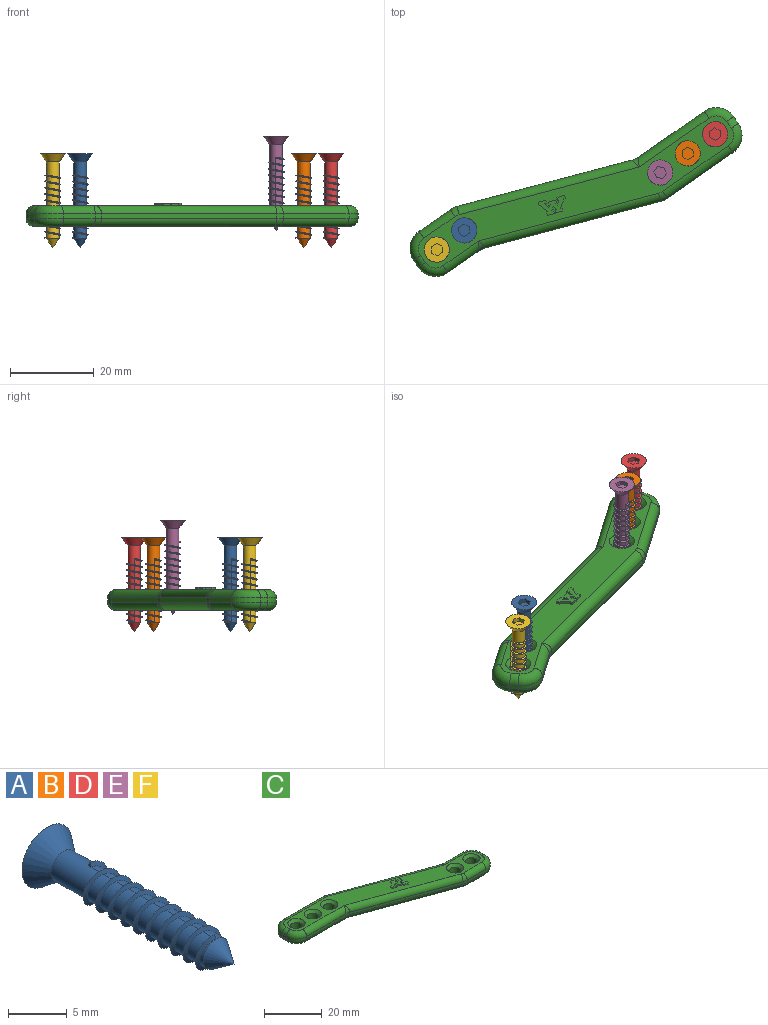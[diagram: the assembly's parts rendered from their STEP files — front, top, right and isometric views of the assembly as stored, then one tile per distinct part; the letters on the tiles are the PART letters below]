
ASSEMBLY  parts=6 mates=5
PART A: 25 faces, bbox 6x22.5x6 mm
  f0: plane 6x6mm, normal (0,1,0), area 22.4mm2, adj f12,f18,f19,f20,f21,f22,f23
  f1: cylinder r=1.5mm len=4.5mm, axis (0,1,0), area 35.3mm2, adj f2,f12,f13,f15
  f2: cylinder r=1.5mm len=3mm, axis (0,1,0), area 11.3mm2, adj f1,f3,f15,f16
  f3: cylinder r=1.5mm len=3mm, axis (0,1,0), area 11.3mm2, adj f2,f4,f15,f16
  f4: cylinder r=1.5mm len=3mm, axis (0,1,0), area 11.3mm2, adj f3,f5,f15,f16
  f5: cylinder r=1.5mm len=3mm, axis (0,1,0), area 11.3mm2, adj f4,f6,f15,f16
  f6: cylinder r=1.5mm len=3mm, axis (0,1,0), area 11.3mm2, adj f5,f7,f15,f16
  f7: cylinder r=1.5mm len=3mm, axis (0,1,0), area 11.3mm2, adj f6,f8,f15,f16
  f8: cylinder r=1.5mm len=3mm, axis (0,1,0), area 11.3mm2, adj f7,f9,f15,f16
  f9: cylinder r=1.5mm len=3mm, axis (0,1,0), area 11.3mm2, adj f8,f10,f15,f16
  f10: cylinder r=1.5mm len=3mm, axis (0,1,0), area 11.3mm2, adj f9,f11,f15,f16
  f11: cylinder r=1.5mm len=3mm, axis (0,1,0), area 7.1mm2, adj f10,f14,f16,f17
  f12: cone r=1.5mm half-angle=36.9deg, axis (0,1,0), area 35.3mm2, adj f0,f1
  f13: plane 0.4x0.3mm, normal (-1,0,0), area 0.1mm2, adj f1,f15,f16
  f14: plane 0.4x0.3mm, normal (1,0,0), area 0.1mm2, adj f11,f15,f16
  f15: bspline ~15.15x4.39mm, area 45.9mm2, adj f1,f2,f3,f4,f5,f6,f7,f8
  f16: bspline ~15.15x4.39mm, area 46mm2, adj f2,f3,f4,f5,f6,f7,f8,f9
  f17: cone r=1.5mm half-angle=34.3deg, axis (0,1,0), area 12.5mm2, adj f11
  f18: plane 1.5x1mm, normal (0,0,-1), area 1.5mm2, adj f0,f19,f23,f24
  f19: plane 1.3x1mm, normal (-0.87,0,-0.5), area 1.5mm2, adj f0,f18,f20,f24
  f20: plane 1.3x1mm, normal (-0.87,0,0.5), area 1.5mm2, adj f0,f19,f21,f24
  f21: plane 1.5x1mm, normal (0,0,1), area 1.5mm2, adj f0,f20,f22,f24
  f22: plane 1.3x1mm, normal (0.87,0,0.5), area 1.5mm2, adj f0,f21,f23,f24
  f23: plane 1.3x1mm, normal (0.87,0,-0.5), area 1.5mm2, adj f0,f18,f22,f24
  f24: plane 3x2.6mm, normal (0,1,0), area 5.8mm2, adj f18,f19,f20,f21,f22,f23
PART B: same geometry as A
PART C: 94 faces, bbox 83.1x28.2x5.6 mm
  f0: plane 78.29x23.39mm, normal (0,0,1), area 452.6mm2, adj f23,f24,f25,f26,f27,f28,f29,f30
  f1: plane 78.29x23.39mm, normal (0,0,-1), area 544.8mm2, adj f10,f11,f12,f13,f14,f15,f16,f17
  f2: plane 2x1mm, normal (-1,0,0), area 2mm2, adj f18,f26,f44,f47
  f3: plane 19.12x1mm, normal (0,-1,0), area 19.1mm2, adj f16,f24,f47,f50
  f4: plane 40.63x14.79mm, normal (-0.34,-0.94,0), area 43.2mm2, adj f15,f23,f41,f50
  f5: plane 9.12x1mm, normal (0,-1,0), area 9.1mm2, adj f17,f25,f38,f41
  f6: plane 2x1mm, normal (1,0,0), area 2mm2, adj f19,f27,f35,f38
  f7: plane 9.12x1mm, normal (0,1,0), area 9.1mm2, adj f21,f29,f35,f53
  f8: plane 40.63x14.79mm, normal (0.34,0.94,0), area 43.2mm2, adj f22,f30,f32,f53
  f9: plane 19.12x1mm, normal (0,1,0), area 19.1mm2, adj f20,f28,f32,f44
  f10: cylinder r=2mm len=4mm, axis (0,0,1), area 50.3mm2, adj f1,f55
  f11: cylinder r=2mm len=4mm, axis (0,0,1), area 50.3mm2, adj f1,f58
  f12: cylinder r=2mm len=4mm, axis (0,0,1), area 50.3mm2, adj f1,f59
  f13: cylinder r=2mm len=4mm, axis (0,0,1), area 50.3mm2, adj f1,f56
  f14: cylinder r=2mm len=4mm, axis (0,0,1), area 50.3mm2, adj f1,f57
  f15: cylinder r=2mm len=42.47mm, axis (0.94,-0.34,0), area 137.2mm2, adj f1,f4,f42,f49
  f16: cylinder r=2mm len=20.35mm, axis (1,0,0), area 61.5mm2, adj f1,f3,f48,f49
  f17: cylinder r=2mm len=9.12mm, axis (1,0,0), area 28.6mm2, adj f1,f5,f39,f42
  f18: cylinder r=2mm len=2mm, axis (0,-1,0), area 6.3mm2, adj f1,f2,f45,f48
  f19: cylinder r=2mm len=2mm, axis (0,1,0), area 6.3mm2, adj f1,f6,f36,f39
  f20: cylinder r=2mm len=19.12mm, axis (-1,0,0), area 60.1mm2, adj f1,f9,f33,f45
  f21: cylinder r=2mm len=10.35mm, axis (-1,0,0), area 30.1mm2, adj f1,f7,f36,f52
  f22: cylinder r=2mm len=42.47mm, axis (-0.94,0.34,0), area 137.2mm2, adj f1,f8,f33,f52
  f23: cylinder r=2mm len=42.47mm, axis (-0.94,0.34,0), area 137.2mm2, adj f0,f4,f40,f51
  f24: cylinder r=2mm len=20.35mm, axis (-1,0,0), area 61.5mm2, adj f0,f3,f46,f51
  f25: cylinder r=2mm len=9.12mm, axis (-1,0,0), area 28.6mm2, adj f0,f5,f37,f40
  f26: cylinder r=2mm len=2mm, axis (0,1,0), area 6.3mm2, adj f0,f2,f43,f46
  f27: cylinder r=2mm len=2mm, axis (0,-1,0), area 6.3mm2, adj f0,f6,f34,f37
  f28: cylinder r=2mm len=19.12mm, axis (1,0,0), area 60.1mm2, adj f0,f9,f31,f43
  f29: cylinder r=2mm len=10.35mm, axis (1,0,0), area 30.1mm2, adj f0,f7,f34,f54
  f30: cylinder r=2mm len=42.47mm, axis (0.94,-0.34,0), area 137.2mm2, adj f0,f8,f31,f54
  f31: torus R=3mm, axis (0,0,1), area 4.7mm2, adj f0,f28,f30,f32
  f32: cylinder r=5mm len=1.71mm, axis (0,0,-1), area 1.7mm2, adj f8,f9,f31,f33
  f33: torus R=3mm, axis (0,0,1), area 4.7mm2, adj f1,f20,f22,f32
  f34: torus R=3mm, axis (0,0,1), area 21.1mm2, adj f0,f27,f29,f35
  f35: cylinder r=5mm len=5mm, axis (0,0,1), area 7.9mm2, adj f6,f7,f34,f36
  f36: torus R=3mm, axis (0,0,1), area 21.1mm2, adj f1,f19,f21,f35
  f37: torus R=3mm, axis (0,0,1), area 21.1mm2, adj f0,f25,f27,f38
  f38: cylinder r=5mm len=5mm, axis (0,0,-1), area 7.9mm2, adj f5,f6,f37,f39
  f39: torus R=3mm, axis (0,0,1), area 21.1mm2, adj f1,f17,f19,f38
  f40: torus R=3mm, axis (0,0,1), area 4.7mm2, adj f0,f23,f25,f41
  f41: cylinder r=5mm len=1.71mm, axis (0,0,-1), area 1.7mm2, adj f4,f5,f40,f42
  f42: torus R=3mm, axis (0,0,1), area 4.7mm2, adj f1,f15,f17,f41
  f43: torus R=3mm, axis (0,0,1), area 21.1mm2, adj f0,f26,f28,f44
  f44: cylinder r=5mm len=5mm, axis (0,0,1), area 7.9mm2, adj f2,f9,f43,f45
  f45: torus R=3mm, axis (0,0,1), area 21.1mm2, adj f1,f18,f20,f44
  f46: torus R=3mm, axis (0,0,1), area 21.1mm2, adj f0,f24,f26,f47
  f47: cylinder r=5mm len=5mm, axis (0,0,-1), area 7.9mm2, adj f2,f3,f46,f48
  f48: torus R=3mm, axis (0,0,1), area 21.1mm2, adj f1,f16,f18,f47
  f49: bspline ~2.3x2.26mm, area 3.5mm2, adj f15,f16,f50
  f50: cylinder r=5mm len=1.71mm, axis (0,0,1), area 1.7mm2, adj f3,f4,f49,f51
  f51: bspline ~2.3x2.26mm, area 3.5mm2, adj f23,f24,f50
  f52: bspline ~2.3x2.26mm, area 3.5mm2, adj f21,f22,f53
  f53: cylinder r=5mm len=1.71mm, axis (0,0,1), area 1.7mm2, adj f7,f8,f52,f54
  f54: bspline ~2.3x2.26mm, area 3.5mm2, adj f29,f30,f53
  f55: cone r=2mm half-angle=45deg, axis (0,0,1), area 22.2mm2, adj f0,f10
  f56: cone r=2mm half-angle=45deg, axis (0,0,1), area 22.2mm2, adj f0,f13
  f57: cone r=2mm half-angle=45deg, axis (0,0,1), area 22.2mm2, adj f0,f14
  f58: cone r=2mm half-angle=45deg, axis (0,0,1), area 22.2mm2, adj f0,f11
  f59: cone r=2mm half-angle=45deg, axis (0,0,1), area 22.2mm2, adj f0,f12
  f60: plane 2.01x1.45mm, normal (-0.59,0.81,0), area 1.5mm2, adj f0,f61,f92,f93
  f61: plane 0.6x0.38mm, normal (0.39,0.92,0), area 0.2mm2, adj f0,f60,f62,f93
  f62: plane 0.75x0.6mm, normal (-0.94,0.33,0), area 0.5mm2, adj f0,f61,f63,f93
  f63: plane 1.79x0.65mm, normal (-0.34,-0.94,0), area 1.1mm2, adj f0,f62,f64,f93
  f64: plane 0.75x0.6mm, normal (0.94,-0.34,0), area 0.5mm2, adj f0,f63,f65,f93
  f65: plane 0.6x0.27mm, normal (0.34,0.94,0), area 0.2mm2, adj f0,f64,f66,f93
  f66: plane 1.01x0.73mm, normal (0.59,-0.81,0), area 0.8mm2, adj f0,f65,f67,f93
  f67: plane 0.6x0.51mm, normal (-0.98,-0.2,0), area 0.3mm2, adj f0,f66,f68,f93
  f68: plane 0.6x0.36mm, normal (0.34,0.94,0), area 0.2mm2, adj f0,f67,f69,f93
  f69: plane 0.79x0.6mm, normal (-0.94,0.34,0), area 0.5mm2, adj f0,f68,f70,f93
  f70: plane 1.91x0.69mm, normal (-0.34,-0.94,0), area 1.2mm2, adj f0,f69,f71,f93
  f71: plane 0.69x0.6mm, normal (0.94,-0.34,0), area 0.4mm2, adj f0,f70,f72,f93
  f72: plane 0.6x0.27mm, normal (0.34,0.94,0), area 0.2mm2, adj f0,f71,f73,f93
  f73: plane 0.65x0.6mm, normal (0.6,-0.8,0), area 0.5mm2, adj f0,f72,f74,f93
  f74: plane 1.43x0.6mm, normal (-0.98,-0.17,0), area 0.9mm2, adj f0,f73,f75,f93
  f75: plane 0.6x0.46mm, normal (0.34,0.94,0), area 0.3mm2, adj f0,f74,f76,f93
  f76: plane 0.68x0.6mm, normal (-0.94,0.34,0), area 0.4mm2, adj f0,f75,f77,f93
  f77: plane 1.79x0.65mm, normal (-0.34,-0.94,0), area 1.1mm2, adj f0,f76,f78,f93
  f78: plane 0.84x0.6mm, normal (0.94,-0.34,0), area 0.5mm2, adj f0,f77,f79,f93
  f79: plane 0.6x0.31mm, normal (0.34,0.94,0), area 0.2mm2, adj f0,f78,f80,f93
  f80: plane 2.21x0.61mm, normal (0.96,0.27,0), area 1.4mm2, adj f0,f79,f81,f93
  f81: plane 0.6x0.3mm, normal (-0.51,-0.86,0), area 0.2mm2, adj f0,f80,f82,f93
  f82: plane 0.84x0.6mm, normal (0.94,-0.34,0), area 0.5mm2, adj f0,f81,f83,f93
  f83: plane 1.67x0.61mm, normal (0.34,0.94,0), area 1.1mm2, adj f0,f82,f84,f93
  f84: plane 0.85x0.6mm, normal (-0.94,0.34,0), area 0.5mm2, adj f0,f83,f85,f93
  f85: plane 0.6x0.41mm, normal (-0.34,-0.94,0), area 0.3mm2, adj f0,f84,f86,f93
  f86: plane 0.81x0.6mm, normal (-0.59,0.81,0), area 0.6mm2, adj f0,f85,f87,f93
  f87: plane 1.05x0.6mm, normal (0.98,0.2,0), area 0.6mm2, adj f0,f86,f88,f93
  f88: plane 0.6x0.33mm, normal (-0.34,-0.94,0), area 0.2mm2, adj f0,f87,f89,f93
  f89: plane 0.74x0.6mm, normal (0.94,-0.34,0), area 0.5mm2, adj f0,f88,f90,f93
  f90: plane 1.64x0.6mm, normal (0.34,0.94,0), area 1mm2, adj f0,f89,f91,f93
  f91: plane 0.69x0.6mm, normal (-0.94,0.34,0), area 0.4mm2, adj f0,f90,f92,f93
  f92: plane 0.6x0.42mm, normal (-0.34,-0.94,0), area 0.3mm2, adj f0,f60,f91,f93
  f93: plane 6.43x5.12mm, normal (0,0,1), area 13.7mm2, adj f60,f61,f62,f63,f64,f65,f66,f67
PART D: same geometry as A
PART E: same geometry as A
PART F: same geometry as A
PLACE A rot(axis=(0.61,-0.56,-0.56),117.3deg) t=(-51.73,-27.42,-25.34)mm
PLACE B rot(axis=(0.61,-0.56,-0.56),117.3deg) t=(1.62,-9.03,-25.34)mm
PLACE C rot(axis=(0,0,-1),145.2deg) t=(16.53,-5.95,-42.74)mm
PLACE D rot(axis=(0.61,-0.56,-0.56),117.3deg) t=(8.18,-4.46,-25.34)mm
PLACE E rot(axis=(1,-0.04,-0.04),90.1deg) t=(-4.95,-13.6,-21.18)mm
PLACE F rot(axis=(0.61,-0.56,-0.56),117.3deg) t=(-58.29,-31.99,-25.34)mm
MATE cylindrical B.f1 <-> C.f11  axis (0,0,1) through (1.62,-9.03,-36.49)mm
MATE cylindrical F.f1 <-> C.f10  axis (0,0,1) through (-58.29,-31.99,-36.49)mm
MATE cylindrical E.f1 <-> C.f12  axis (0,0,1) through (-4.95,-13.6,-32.33)mm
MATE cylindrical D.f1 <-> C.f14  axis (0,0,1) through (8.18,-4.46,-36.49)mm
MATE cylindrical A.f1 <-> C.f13  axis (0,0,1) through (-51.73,-27.42,-36.49)mm
